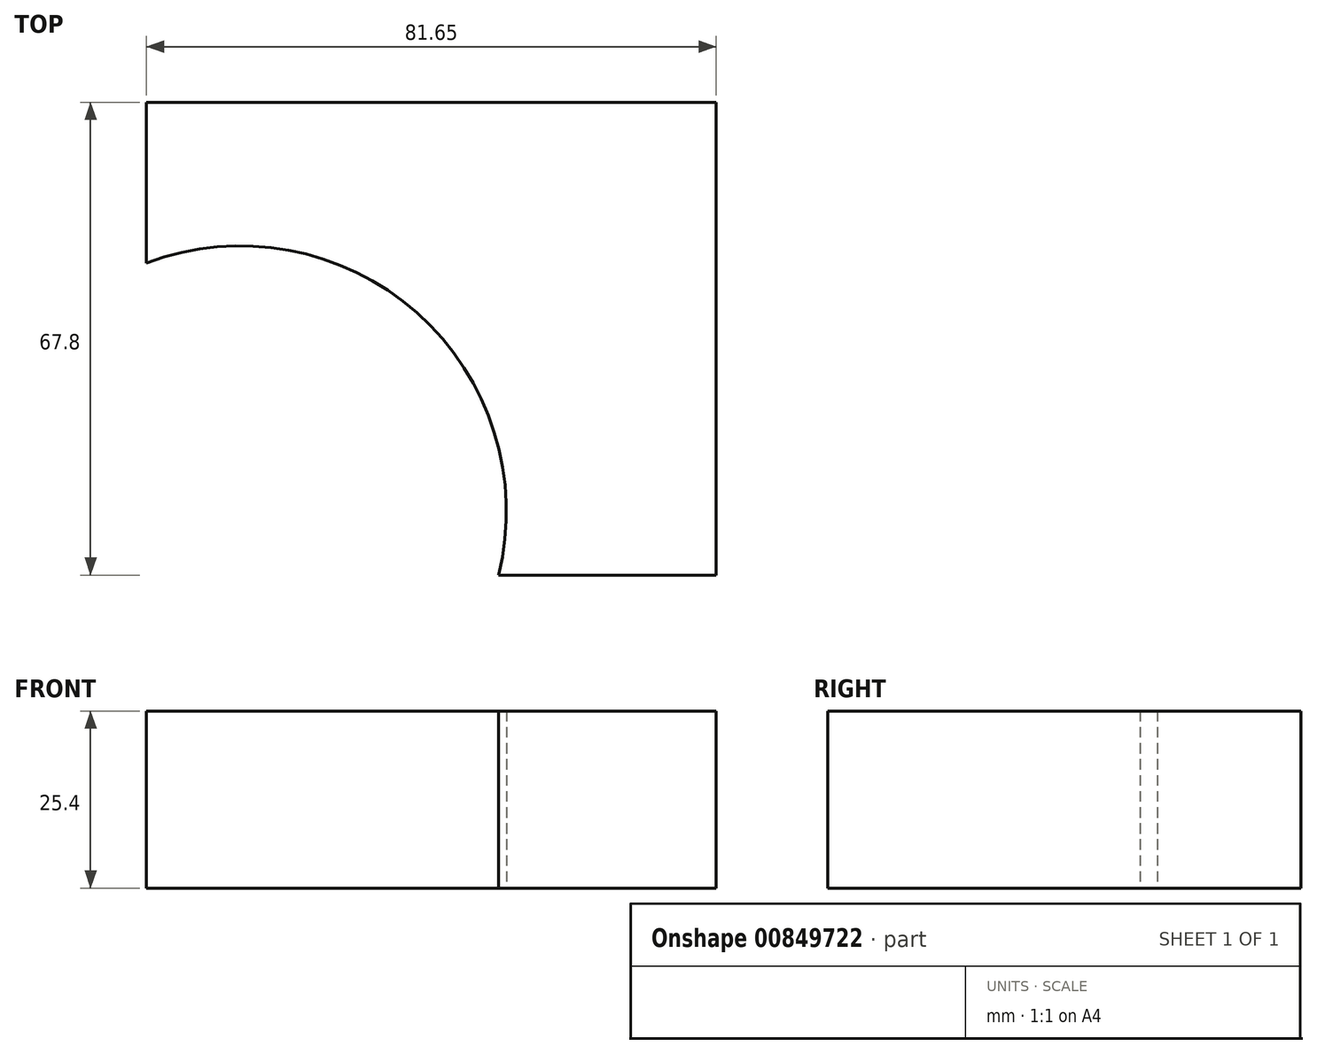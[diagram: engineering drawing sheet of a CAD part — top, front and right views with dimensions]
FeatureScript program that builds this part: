
annotation { "Feature Type Name" : "Feature", "Feature Type Description" : "" }
export const myFeature = defineFeature(function(context is Context, id is Id, definition is map)
    precondition{}
    {
        {
            var Q0;
            Q0=qCreatedBy(makeId("Top.planeOp"),FACE);
            var sketch = newSketch(context, id + "F0", { "sketchPlane" : qUnion([Q0])});
            skLineSegment(sketch, "E0.bottom", {"start": v(-40.37, 36.18) * mm, "end": v(41.28, 36.18) * mm});
            skLineSegment(sketch, "E0.top", {"start": v(-40.37, -31.62) * mm, "end": v(41.28, -31.62) * mm});
            skLineSegment(sketch, "E0.left", {"start": v(-40.37, 36.18) * mm, "end": v(-40.37, -31.62) * mm});
            skLineSegment(sketch, "E0.right", {"start": v(41.28, 36.18) * mm, "end": v(41.28, -31.62) * mm});
            skPoint(sketch, "E1", {"position": v(27.43, 0) * mm});
            skPoint(sketch, "E2", {"position": v(-25.79, 0) * mm});
            skPoint(sketch, "E3", {"position": v(0, 28.52) * mm});
            skPoint(sketch, "E4", {"position": v(0, -17.4) * mm});
            skSolve(sketch);
        }
        {
            var Q0;
            Q0=makeQuery(id+"F0.imprint","IMPRINT",FACE,{"disambiguationData":[TD([[makeQuery(id+"F0.imprint","IMPRINT",EDGE,{"derivedFrom":sQuery(id+"F0.wireOp",EDGE,"E0.bottom")}),-1.0]])]});
            extrude(context, id + "F1", {"entities" : qUnion([Q0]), "depth" : 25.4 * mm, "offsetDistance" : 25.4 * mm});
        }
        {
            var Q0;
            Q0=qCreatedBy(makeId("Top.planeOp"),FACE);
            var sketch = newSketch(context, id + "F2", { "sketchPlane" : qUnion([Q0])});
            skPoint(sketch, "E5", {"position": v(-26.88, -22.5) * mm});
            skPoint(sketch, "E6", {"position": v(20.5, -18.5) * mm});
            skPoint(sketch, "E7", {"position": v(-21.6, 22.5) * mm});
            skPoint(sketch, "E8", {"position": v(26.15, 20.5) * mm});
            skSolve(sketch);
        }
        {
            var Q0;
            Q0=sQuery(id+"F2.wireOp",VERTEX,"E5");
            var Q1;
            Q1=makeQuery(id+"F1.opExtrude","SWEPT_BODY",BODY,{"disambiguationData":[OSD([sQuery(id+"F0.wireOp",EDGE,"E0.bottom"),sQuery(id+"F0.wireOp",EDGE,"E0.top"),sQuery(id+"F0.wireOp",EDGE,"E0.left"),sQuery(id+"F0.wireOp",EDGE,"E0.right")])]});
            hole(context, id + "F3", {"style" : HoleStyle.SIMPLE, "endStyle" : HoleEndStyle.THROUGH, "oppositeDirection" : true, "holeDiameter" : 76.2 * mm, "majorDiameter" : 6.35 * mm, "isTappedThrough" : true, "tappedDepth" : 12.7 * mm, "tapClearance" : 3, "locations" : qUnion([Q0]), "scope" : qUnion([Q1])});
        }
    });
